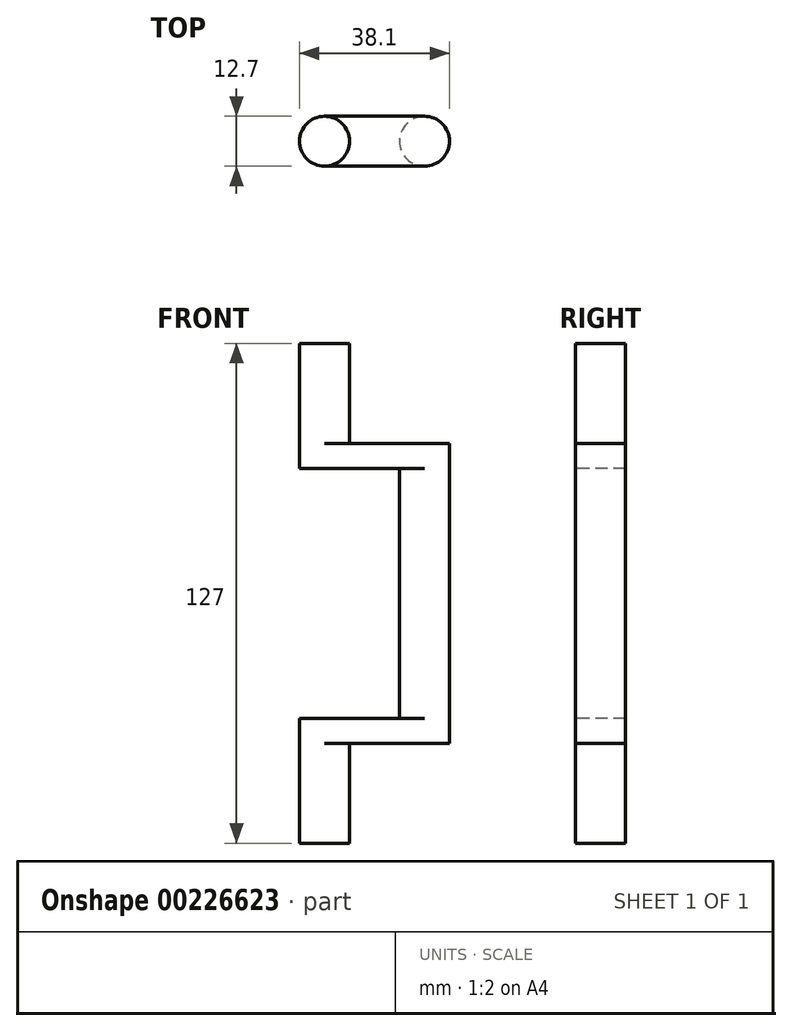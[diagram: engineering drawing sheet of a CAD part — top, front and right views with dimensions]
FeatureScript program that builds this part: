
annotation { "Feature Type Name" : "Feature", "Feature Type Description" : "" }
export const myFeature = defineFeature(function(context is Context, id is Id, definition is map)
    precondition{}
    {
        {
            var Q0;
            Q0=qCreatedBy(makeId("Top.planeOp"),FACE);
            var sketch = newSketch(context, id + "F0", { "sketchPlane" : qUnion([Q0])});
            skCircle(sketch, "E0", {"center": v(0, 0) * mm, "radius": 6.35 * mm});
            skSolve(sketch);
        }
        {
            var Q0;
            Q0 = qSketchRegion(id + "F0", true);
            extrude(context, id + "F1", {"entities" : qUnion([Q0]), "depth" : 25.4 * mm});
        }
        {
            var Q0;
            Q0=makeQuery(id+"F1.opExtrude","CAP_FACE",FACE,{"disambiguationData":[OSD([sQuery(id+"F0.wireOp",EDGE,"E0")])],"isStart":false});
            var sketch = newSketch(context, id + "F2", { "sketchPlane" : qUnion([Q0])});
            skArc(sketch, "E1.0", {"start": v(0, 6.35) * mm, "mid": v(-6.35, 0) * mm, "end": v(0, -6.35) * mm});
            skLineSegment(sketch, "E2.bottom", {"start": v(0, 6.35) * mm, "end": v(25.4, 6.35) * mm});
            skLineSegment(sketch, "E2.top", {"start": v(0, -6.35) * mm, "end": v(25.4, -6.35) * mm});
            skLineSegment(sketch, "E2.left", {"start": v(0, 6.35) * mm, "end": v(0, -6.35) * mm, "construction": true});
            skLineSegment(sketch, "E2.right", {"start": v(25.4, 6.35) * mm, "end": v(25.4, -6.35) * mm, "construction": true});
            skArc(sketch, "E3", {"start": v(25.4, -6.35) * mm, "mid": v(31.75, 0) * mm, "end": v(25.4, 6.35) * mm});
            skSolve(sketch);
        }
        {
            var Q0;
            Q0 = qSketchRegion(id + "F2", true);
            extrude(context, id + "F3", {"entities" : qUnion([Q0]), "operationType" : NewBodyOperationType.ADD, "depth" : 6.35 * mm});
        }
        {
            var Q0;
            Q0=makeQuery(id+"F3.opExtrude","CAP_FACE",FACE,{"disambiguationData":[OSD([sQuery(id+"F2.wireOp",EDGE,"E1.0"),sQuery(id+"F2.wireOp",EDGE,"E2.bottom"),sQuery(id+"F2.wireOp",EDGE,"E2.top"),sQuery(id+"F2.wireOp",EDGE,"E3")])],"isStart":false});
            var sketch = newSketch(context, id + "F4", { "sketchPlane" : qUnion([Q0])});
            skCircle(sketch, "E4", {"center": v(25.4, 0) * mm, "radius": 6.35 * mm});
            skSolve(sketch);
        }
        {
            var Q0;
            Q0 = qSketchRegion(id + "F4", true);
            extrude(context, id + "F5", {"entities" : qUnion([Q0]), "operationType" : NewBodyOperationType.ADD, "depth" : 31.75 * mm});
        }
        {
            var Q0;
            Q0=makeQuery(id+"F1.opExtrude","SWEPT_BODY",BODY,{"disambiguationData":[OSD([sQuery(id+"F0.wireOp",EDGE,"E0")])]});
            var Q1;
            Q1=makeQuery(id+"F5.opExtrude","CAP_FACE",FACE,{"disambiguationData":[OSD([sQuery(id+"F4.wireOp",EDGE,"E4")])],"isStart":false});
            mirror(context, id + "F6", {"operationType" : NewBodyOperationType.ADD, "entities" : qUnion([Q0]), "mirrorPlane" : qUnion([Q1])});
        }
    });
